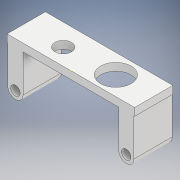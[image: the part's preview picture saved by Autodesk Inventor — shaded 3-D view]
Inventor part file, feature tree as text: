
AUTODESK INVENTOR PART (.ipt)
format: ipt  version: 2018 (Build 220112000, 112)  size: 152,576 bytes
history: native  units: mm
features: extrude x3, sketch x3, projected_geometry x1
ambient origin geometry x8: Origin, YZ Plane, XZ Plane, XY Plane, X Axis, Y Axis, Z Axis, Center Point
bodies: Solid1 (feature_tree)
feature tree (7):
  extrude  "Extrusion1"  Depth=50.0mm
  sketch  "Sketch2"  dims[d2=43.5mm d3=14.635741mm]
  extrude  "Extrusion2"  Depth=43.5mm
  sketch  "Sketch3"  dims[d4=3.7mm d5=3.0mm d6=15.0mm d7=0.0mm d8=6.5mm d9=12.7mm d10=0.0mm d14=34.5mm d15=8.5mm d16=12.0mm d17=8.5mm d18=10.0mm d19=0.0mm d21=15.0mm d22=7.4mm]
  extrude  "Extrusion3"  Depth=3.0mm
  sketch  "Sketch1"  dims[d0=3.0mm d1=50.0mm]
  projected_geometry  "Projected Loop1"
